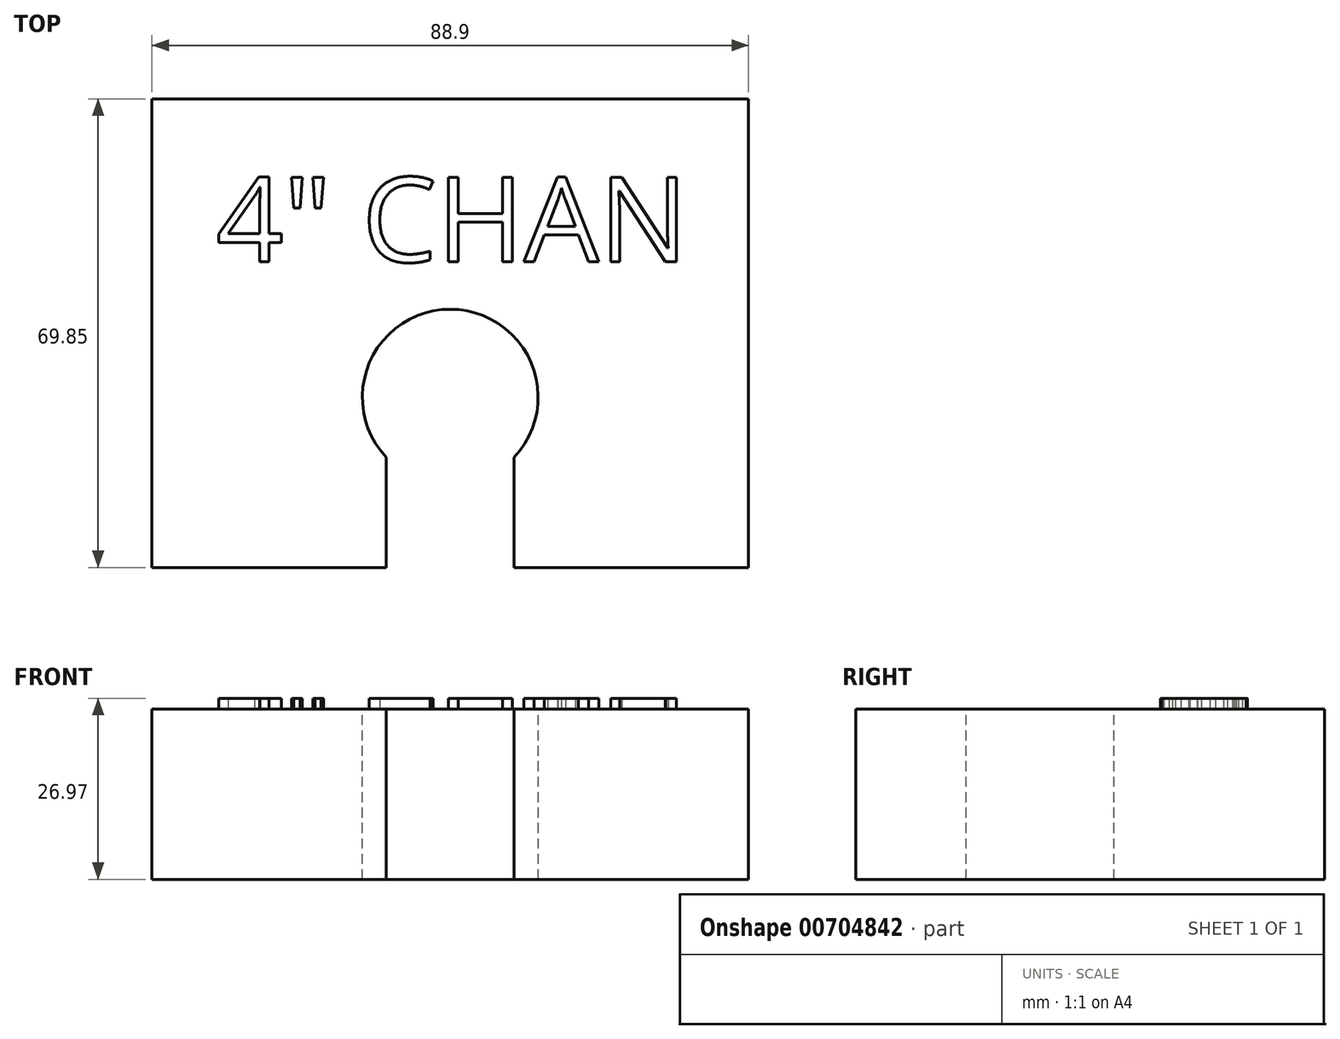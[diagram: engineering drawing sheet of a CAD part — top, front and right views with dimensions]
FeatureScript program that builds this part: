
annotation { "Feature Type Name" : "Feature", "Feature Type Description" : "" }
export const myFeature = defineFeature(function(context is Context, id is Id, definition is map)
    precondition{}
    {
        {
            var Q0;
            Q0=qCreatedBy(makeId("Top.planeOp"),FACE);
            var sketch = newSketch(context, id + "F0", { "sketchPlane" : qUnion([Q0])});
            skLineSegment(sketch, "E0.bottom", {"start": v(-53.09, 49.19) * mm, "end": v(35.81, 49.19) * mm});
            skLineSegment(sketch, "E0.top", {"start": v(-53.09, -20.66) * mm, "end": v(35.81, -20.66) * mm});
            skLineSegment(sketch, "E0.left", {"start": v(-53.09, 49.19) * mm, "end": v(-53.09, -20.66) * mm});
            skLineSegment(sketch, "E0.right", {"start": v(35.81, 49.19) * mm, "end": v(35.81, -20.66) * mm});
            skSolve(sketch);
        }
        {
            var Q0;
            Q0=makeQuery(id+"F0.imprint","IMPRINT",FACE,{"disambiguationData":[TD([[makeQuery(id+"F0.imprint","IMPRINT",EDGE,{"derivedFrom":sQuery(id+"F0.wireOp",EDGE,"E0.bottom")}),-1.0]])]});
            extrude(context, id + "F1", {"entities" : qUnion([Q0]), "depth" : 25.4 * mm, "offsetDistance" : 25.4 * mm});
        }
        {
            var Q0;
            Q0=makeQuery(id+"F1.opExtrude","CAP_FACE",FACE,{"disambiguationData":[OSD([sQuery(id+"F0.wireOp",EDGE,"E0.bottom"),sQuery(id+"F0.wireOp",EDGE,"E0.top"),sQuery(id+"F0.wireOp",EDGE,"E0.left"),sQuery(id+"F0.wireOp",EDGE,"E0.right")])],"isStart":false});
            var sketch = newSketch(context, id + "F2", { "sketchPlane" : qUnion([Q0])});
            skPoint(sketch, "E1", {"position": v(-8.64, 4.74) * mm});
            skPoint(sketch, "E1.positionSnap0", {"position": v(-8.64, -20.66) * mm});
            skArc(sketch, "E2", {"start": v(0.89, -4.25) * mm, "mid": v(-8.64, 17.84) * mm, "end": v(-18.16, -4.25) * mm});
            skLineSegment(sketch, "E3.0", {"start": v(-18.16, -4.25) * mm, "end": v(-18.16, -20.66) * mm});
            skLineSegment(sketch, "E4.0", {"start": v(0.89, -4.25) * mm, "end": v(0.89, -20.66) * mm});
            skSolve(sketch);
        }
        {
            var Q0;
            Q0=makeQuery(id+"F2.imprint","IMPRINT",FACE,{"disambiguationData":[TD([[makeQuery(id+"F2.imprint","IMPRINT",EDGE,{"derivedFrom":sQuery(id+"F2.wireOp",EDGE,"E2")}),1.0]])]});
            extrude(context, id + "F3", {"entities" : qUnion([Q0]), "operationType" : NewBodyOperationType.REMOVE, "oppositeDirection" : true, "depth" : 25.4 * mm, "offsetDistance" : 25.4 * mm});
        }
        {
            var Q0;
            Q0=makeQuery(id+"F1.opExtrude","CAP_FACE",FACE,{"disambiguationData":[OSD([sQuery(id+"F0.wireOp",EDGE,"E0.bottom"),sQuery(id+"F0.wireOp",EDGE,"E0.top"),sQuery(id+"F0.wireOp",EDGE,"E0.left"),sQuery(id+"F0.wireOp",EDGE,"E0.right")])],"isStart":false});
            var sketch = newSketch(context, id + "F4", { "sketchPlane" : qUnion([Q0])});
            skText(sketch, "E5", { "text": "4\" CHAN", "fontName": "OpenSans-Regular.ttf"});
            skPoint(sketch, "E6", {"position": v(-8.64, 49.19) * mm});
            const initialGuessF4  = {"E5": [-0.04352, 0.02489, 1, 0, 0.0127]};
            skSetInitialGuess(sketch, initialGuessF4);
            skSolve(sketch);
        }
        {
            var Q0;
            Q0 = qSketchRegion(id + "F4", true);
            extrude(context, id + "F5", {"entities" : qUnion([Q0]), "operationType" : NewBodyOperationType.ADD, "depth" : 1.57 * mm, "offsetDistance" : 25.4 * mm});
        }
    });
